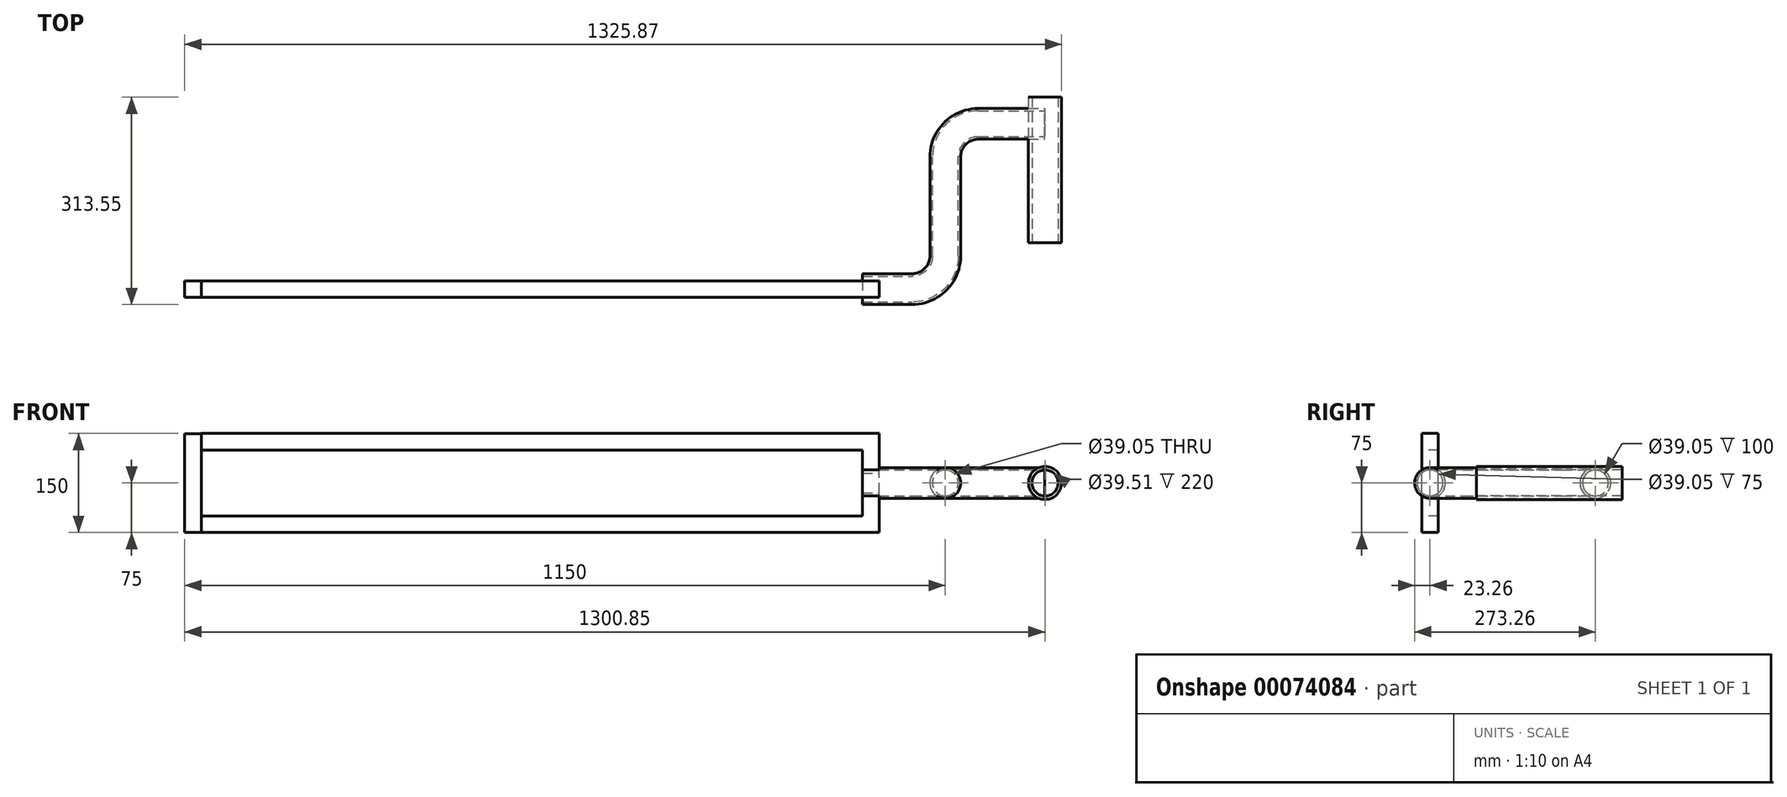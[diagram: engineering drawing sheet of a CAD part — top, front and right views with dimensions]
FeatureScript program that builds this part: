
annotation { "Feature Type Name" : "Feature", "Feature Type Description" : "" }
export const myFeature = defineFeature(function(context is Context, id is Id, definition is map)
    precondition{}
    {
        {
            var Q0;
            Q0=qCreatedBy(makeId("Top.planeOp"),FACE);
            var sketch = newSketch(context, id + "F0", { "sketchPlane" : qUnion([Q0])});
            skLineSegment(sketch, "E0", {"start": v(-2.73, 0) * mm, "end": v(47.27, 0) * mm});
            skLineSegment(sketch, "E1", {"start": v(97.27, 50) * mm, "end": v(97.27, 200) * mm});
            skLineSegment(sketch, "E2", {"start": v(147.27, 250) * mm, "end": v(247.27, 250) * mm});
            skPoint(sketch, "E3.visualSharp", {"position": v(97.27, 0) * mm});
            skArc(sketch, "E3.filletArc", {"start": v(47.27, 0) * mm, "mid": v(82.62, 14.64) * mm, "end": v(97.27, 50) * mm});
            skPoint(sketch, "E4.visualSharp", {"position": v(97.27, 250) * mm});
            skArc(sketch, "E4.filletArc", {"start": v(147.27, 250) * mm, "mid": v(111.91, 235.36) * mm, "end": v(97.27, 200) * mm});
            skSolve(sketch);
        }
        {
            var Q0;
            Q0=sQuery(id+"F0.wireOp",VERTEX,"E0.start");
            var Q1;
            Q1=sQuery(id+"F0.wireOp",EDGE,"E0");
            cPlane(context, id + "F1", {"entities" : qUnion([Q0, Q1]), "cplaneType" : CPlaneType.LINE_POINT, "offset" : 150 * mm, "width" : 150 * mm, "height" : 150 * mm});
        }
        {
            var Q0;
            Q0=qCreatedBy(id+"F1.planeOp",FACE);
            var sketch = newSketch(context, id + "F2", { "sketchPlane" : qUnion([Q0])});
            skCircle(sketch, "E5", {"center": v(0, 0) * mm, "radius": 23.26 * mm});
            skCircle(sketch, "E6", {"center": v(0, 0) * mm, "radius": 19.52 * mm});
            skSolve(sketch);
        }
        {
            var Q0;
            Q0=makeQuery(id+"F2.imprint","IMPRINT",FACE,{"disambiguationData":[TD([[makeQuery(id+"F2.imprint","IMPRINT",EDGE,{"derivedFrom":sQuery(id+"F2.wireOp",EDGE,"E5")}),1.0]])]});
            var Q1;
            Q1=sQuery(id+"F0.wireOp",EDGE,"E0");
            var Q2;
            Q2=sQuery(id+"F0.wireOp",EDGE,"E3.filletArc");
            var Q3;
            Q3=sQuery(id+"F0.wireOp",EDGE,"E1");
            var Q4;
            Q4=sQuery(id+"F0.wireOp",EDGE,"E4.filletArc");
            var Q5;
            Q5=sQuery(id+"F0.wireOp",EDGE,"E2");
            sweep(context, id + "F3", {"profiles" : qUnion([Q0]), "path" : qUnion([Q1, Q2, Q3, Q4, Q5])});
        }
        {
            var Q0;
            Q0=makeQuery(id+"F3.opSweep","CAP_FACE",FACE,{"disambiguationData":[OSD([sQuery(id+"F0.wireOp",VERTEX,"E2.end"),sQuery(id+"F2.wireOp",EDGE,"E5")])],"isStart":false});
            var sketch = newSketch(context, id + "F4", { "sketchPlane" : qUnion([Q0])});
            skLineSegment(sketch, "E7", {"start": v(250, 0) * mm, "end": v(70.29, 0) * mm});
            skSolve(sketch);
        }
        {
            var Q0;
            Q0=sQuery(id+"F4.wireOp",EDGE,"E7");
            var Q1;
            Q1=sQuery(id+"F4.wireOp",VERTEX,"E7.end");
            cPlane(context, id + "F5", {"entities" : qUnion([Q0, Q1]), "cplaneType" : CPlaneType.LINE_POINT, "offset" : 150 * mm, "width" : 150 * mm, "height" : 150 * mm});
        }
        {
            var Q0;
            Q0=qCreatedBy(id+"F5.planeOp",FACE);
            var sketch = newSketch(context, id + "F6", { "sketchPlane" : qUnion([Q0])});
            skCircle(sketch, "E8", {"center": v(248.12, 0) * mm, "radius": 25.02 * mm});
            skCircle(sketch, "E9", {"center": v(248.12, 0) * mm, "radius": 19.75 * mm});
            skSolve(sketch);
        }
        {
            var Q0;
            Q0=makeQuery(id+"F6.imprint","IMPRINT",FACE,{"disambiguationData":[TD([[makeQuery(id+"F6.imprint","IMPRINT",EDGE,{"derivedFrom":sQuery(id+"F6.wireOp",EDGE,"E8")}),1.0]])]});
            extrude(context, id + "F7", {"entities" : qUnion([Q0]), "oppositeDirection" : true, "depth" : 220 * mm});
        }
        {
            var Q0;
            Q0=qCreatedBy(id+"F1.planeOp",FACE);
            var sketch = newSketch(context, id + "F8", { "sketchPlane" : qUnion([Q0])});
            skLineSegment(sketch, "E10.rect.bottom", {"start": v(-12.5, -75) * mm, "end": v(12.5, -75) * mm});
            skLineSegment(sketch, "E10.rect.top", {"start": v(-12.5, 75) * mm, "end": v(12.5, 75) * mm});
            skLineSegment(sketch, "E10.rect.left", {"start": v(-12.5, -75) * mm, "end": v(-12.5, 75) * mm});
            skLineSegment(sketch, "E10.rect.right", {"start": v(12.5, -75) * mm, "end": v(12.5, 75) * mm});
            skPoint(sketch, "E10.rect.middle", {"position": v(0, 0) * mm});
            skSolve(sketch);
        }
        {
            var Q0;
            Q0=makeQuery(id+"F8.imprint","IMPRINT",FACE,{"disambiguationData":[TD([[makeQuery(id+"F8.imprint","IMPRINT",EDGE,{"derivedFrom":sQuery(id+"F8.wireOp",EDGE,"E10.rect.bottom")}),1.0]])]});
            var Q1;
            Q1=makeQuery(id+"F3.opSweep","CAP_FACE",FACE,{"disambiguationData":[OSD([sQuery(id+"F0.wireOp",VERTEX,"E0.start"),sQuery(id+"F2.wireOp",EDGE,"E5"),sQuery(id+"F2.wireOp",EDGE,"E6")])],"isStart":true});
            extrude(context, id + "F9", {"entities" : qUnion([Q0, Q1]), "operationType" : NewBodyOperationType.ADD, "oppositeDirection" : true, "depth" : 25 * mm});
        }
        {
            var Q0;
            Q0=makeQuery(id+"F9.boolean.opBoolean","MERGE",FACE,{"derivedFrom":[makeQuery(id+"F9.opExtrude","CAP_FACE",FACE,{"disambiguationData":[OSD([sQuery(id+"F0.wireOp",VERTEX,"E0.start"),sQuery(id+"F2.wireOp",EDGE,"E5"),sQuery(id+"F2.wireOp",EDGE,"E6")])],"isStart":false}),makeQuery(id+"F9.opExtrude","CAP_FACE",FACE,{"disambiguationData":[OSD([sQuery(id+"F8.wireOp",EDGE,"E10.rect.bottom"),sQuery(id+"F8.wireOp",EDGE,"E10.rect.top"),sQuery(id+"F8.wireOp",EDGE,"E10.rect.left"),sQuery(id+"F8.wireOp",EDGE,"E10.rect.right")])],"isStart":false})]});
            var sketch = newSketch(context, id + "F10", { "sketchPlane" : qUnion([Q0])});
            skLineSegment(sketch, "E11.bottom", {"start": v(-12.5, -75) * mm, "end": v(12.5, -75) * mm});
            skLineSegment(sketch, "E11.top", {"start": v(-12.5, -50) * mm, "end": v(12.5, -50) * mm});
            skLineSegment(sketch, "E11.left", {"start": v(-12.5, -75) * mm, "end": v(-12.5, -50) * mm});
            skLineSegment(sketch, "E11.right", {"start": v(12.5, -75) * mm, "end": v(12.5, -50) * mm});
            skLineSegment(sketch, "E12.bottom", {"start": v(-12.5, 75) * mm, "end": v(12.5, 75) * mm});
            skLineSegment(sketch, "E12.top", {"start": v(-12.5, 50) * mm, "end": v(12.5, 50) * mm});
            skLineSegment(sketch, "E12.left", {"start": v(-12.5, 75) * mm, "end": v(-12.5, 50) * mm});
            skLineSegment(sketch, "E12.right", {"start": v(12.5, 75) * mm, "end": v(12.5, 50) * mm});
            skSolve(sketch);
        }
        {
            var Q0;
            Q0=makeQuery(id+"F10.imprint","IMPRINT",FACE,{"disambiguationData":[TD([[makeQuery(id+"F10.imprint","IMPRINT",EDGE,{"derivedFrom":sQuery(id+"F10.wireOp",EDGE,"E11.bottom")}),-1.0]])]});
            var Q1;
            Q1=makeQuery(id+"F10.imprint","IMPRINT",FACE,{"disambiguationData":[TD([[makeQuery(id+"F10.imprint","IMPRINT",EDGE,{"derivedFrom":sQuery(id+"F10.wireOp",EDGE,"E12.bottom")}),1.0]])]});
            extrude(context, id + "F11", {"entities" : qUnion([Q0, Q1]), "operationType" : NewBodyOperationType.ADD, "depth" : 1000 * mm});
        }
        {
            var Q0;
            Q0=makeQuery(id+"F11.opExtrude","CAP_FACE",FACE,{"disambiguationData":[OSD([sQuery(id+"F10.wireOp",EDGE,"E11.bottom"),sQuery(id+"F10.wireOp",EDGE,"E11.top"),sQuery(id+"F10.wireOp",EDGE,"E11.left"),sQuery(id+"F10.wireOp",EDGE,"E11.right")])],"isStart":false});
            var sketch = newSketch(context, id + "F12", { "sketchPlane" : qUnion([Q0])});
            skLineSegment(sketch, "E13.bottom", {"start": v(-12.5, -75) * mm, "end": v(12.54, -75) * mm});
            skLineSegment(sketch, "E13.top", {"start": v(-12.5, 74.7) * mm, "end": v(12.54, 74.7) * mm});
            skLineSegment(sketch, "E13.left", {"start": v(-12.5, -75) * mm, "end": v(-12.5, 74.7) * mm});
            skLineSegment(sketch, "E13.right", {"start": v(12.54, -75) * mm, "end": v(12.54, 74.7) * mm});
            skSolve(sketch);
        }
        {
            var Q0;
            {var subQ4=makeQuery(id+"F11.opExtrude","CAP_EDGE",EDGE,{"disambiguationData":[OSD([sQuery(id+"F10.wireOp",EDGE,"E11.top")])],"isStart":false});Q0=makeQuery(id+"F12.imprint","IMPRINT",FACE,{"disambiguationData":[TD([[makeQuery(id+"F12.imprint","IMPRINT",EDGE,{"derivedFrom":subQ4}),-1.0]])]});}
            var Q1;
            {var subQ2=sQuery(id+"F12.wireOp",EDGE,"E13.top");Q1=makeQuery(id+"F12.imprint","IMPRINT",FACE,{"disambiguationData":[TD([[makeQuery(id+"F12.imprint","IMPRINT",EDGE,{"derivedFrom":subQ2}),-1.0]])]});}
            var Q2;
            Q2=sQuery(id+"F12.wireOp",EDGE,"E13.left");
            var Q3;
            Q3=sQuery(id+"F12.wireOp",EDGE,"E13.right");
            var Q4;
            Q4=sQuery(id+"F12.wireOp",EDGE,"E13.bottom");
            var Q5;
            Q5=sQuery(id+"F12.wireOp",EDGE,"E13.top");
            extrude(context, id + "F13", {"entities" : qUnion([Q0, Q1]), "surfaceEntities" : qUnion([Q2, Q3, Q4, Q5]), "depth" : 25 * mm});
        }
    });
